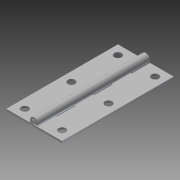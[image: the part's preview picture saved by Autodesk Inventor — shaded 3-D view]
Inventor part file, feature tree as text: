
AUTODESK INVENTOR PART (.ipt)
format: ipt  version: 2014 (Build 180170000, 170)  size: 328,192 bytes
history: native  units: in
note: dims shown in document units (in); Inventor stores cm internally (conversion verified against a paired STEP export)
features: extrude x6, sketch x5, imported_body x3, projected_geometry x3, other x2, chamfer x1
ambient origin geometry x8: Origin, YZ Plane, XZ Plane, XY Plane, X Axis, Y Axis, Z Axis, Center Point
bodies: Body1 (feature_tree), Body2 (feature_tree), Body3 (feature_tree)
feature tree (20):
  other  "LPattern1"
  other  "15665A319 (1)1"
  extrude  "Extrusion2"  Depth=1.5in
  extrude  "Extrusion3"  Depth=1.0in TaperAngle=0.0deg
  extrude  "Extrusion4"  Depth=0.196in
  extrude  "Extrusion5"  Depth=0.25in
  extrude  "Extrusion6"  Depth=1.5in TaperAngle=0.0deg
  chamfer  "Chamfer1"  Distance=1.5in
  extrude  "Extrude5"  Depth=1.5in
  imported_body  "Base1"
  imported_body  "Base2"
  imported_body  "Base3"
  sketch  "Sketch2"  dims[d5=1.5in d6=9.0in]
  sketch  "Sketch3"  dims[d7=1.0in d8=0.0in d9=9.0in d10=0.0in]
  projected_geometry  "Projected Loop1"
  projected_geometry  "Projected Loop2"
  sketch  "Sketch4"  dims[d11=9.0in d12=0.0in d13=0.196in]
  sketch  "Sketch5"  dims[d14=0.25in d15=0.25in]
  sketch  "Sketch6"  dims[d17=0.25in d18=10.25in d19=0.0in d20=1.5in d21=1.75in d22=10.25in d23=0.0in]
  projected_geometry  "Projected Loop3"
